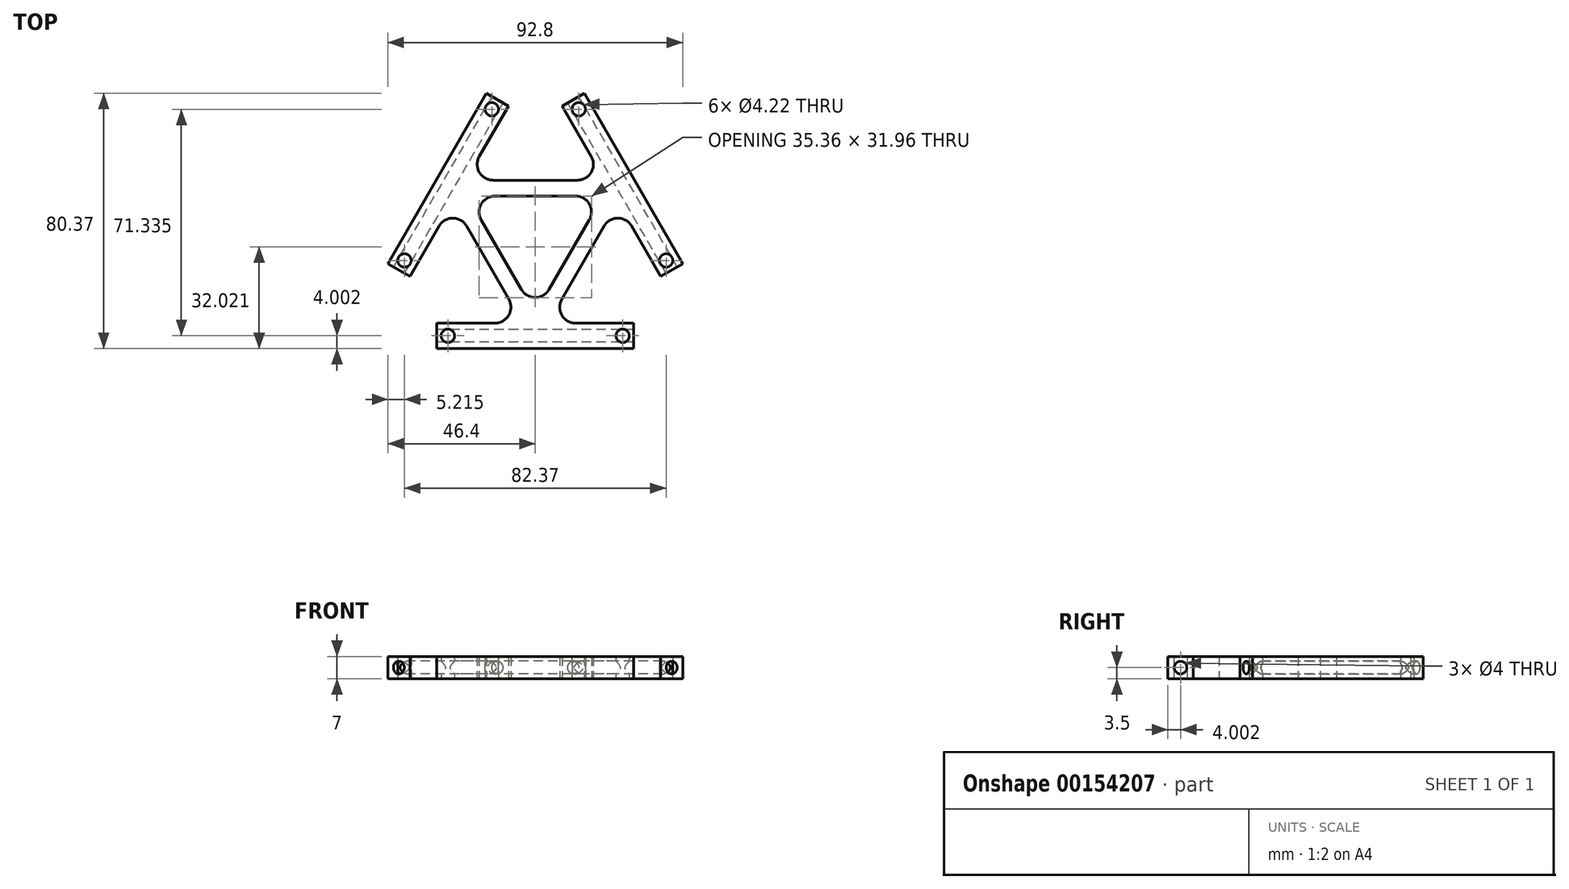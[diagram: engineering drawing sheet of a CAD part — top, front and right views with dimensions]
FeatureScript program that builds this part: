
annotation { "Feature Type Name" : "Feature", "Feature Type Description" : "" }
export const myFeature = defineFeature(function(context is Context, id is Id, definition is map)
    precondition{}
    {
        {
            var Q0;
            Q0=qCreatedBy(makeId("Top.planeOp"),FACE);
            var sketch = newSketch(context, id + "F0", { "sketchPlane" : qUnion([Q0])});
            skLineSegment(sketch, "E0", {"start": v(-8.35, 14.46) * mm, "end": v(-21.65, 37.5) * mm});
            skLineSegment(sketch, "E1", {"start": v(-13.3, 51.96) * mm, "end": v(13.3, 51.96) * mm});
            skLineSegment(sketch, "E2", {"start": v(21.65, 37.5) * mm, "end": v(8.35, 14.46) * mm});
            skLineSegment(sketch, "E3.bottom", {"start": v(-31, 6.96) * mm, "end": v(-12.68, 6.96) * mm});
            skLineSegment(sketch, "E3.top", {"start": v(-31, -1.04) * mm, "end": v(31, -1.04) * mm});
            skLineSegment(sketch, "E3.left", {"start": v(-31, 6.96) * mm, "end": v(-31, -1.04) * mm});
            skLineSegment(sketch, "E3.right", {"start": v(31, 6.96) * mm, "end": v(31, -1.04) * mm});
            skLineSegment(sketch, "E4", {"start": v(-15, 64.02) * mm, "end": v(-17.63, 59.46) * mm});
            skPoint(sketch, "E4.startSnap0", {"position": v(-15, 25.98) * mm});
            skLineSegment(sketch, "E5", {"start": v(-39.47, 21.63) * mm, "end": v(-46.4, 25.63) * mm});
            skLineSegment(sketch, "E6", {"start": v(-46.4, 25.63) * mm, "end": v(-15.4, 79.33) * mm});
            skLineSegment(sketch, "E7", {"start": v(-15.4, 79.33) * mm, "end": v(-8.47, 75.33) * mm});
            skLineSegment(sketch, "E8", {"start": v(39.47, 21.63) * mm, "end": v(30.31, 37.5) * mm});
            skLineSegment(sketch, "E9", {"start": v(8.47, 75.33) * mm, "end": v(15.4, 79.33) * mm});
            skLineSegment(sketch, "E10", {"start": v(15.4, 79.33) * mm, "end": v(46.4, 25.63) * mm});
            skLineSegment(sketch, "E11", {"start": v(46.4, 25.63) * mm, "end": v(39.47, 21.63) * mm});
            skLineSegment(sketch, "E12", {"start": v(-15, 64.02) * mm, "end": v(-8.47, 75.33) * mm});
            skPoint(sketch, "E13.orphan", {"position": v(-30, 51.96) * mm});
            skPoint(sketch, "E14.orphan", {"position": v(0, 0) * mm});
            skPoint(sketch, "E15.orphan", {"position": v(30, 51.96) * mm});
            skLineSegment(sketch, "E16.trimOffspring", {"start": v(-30.31, 37.5) * mm, "end": v(-39.47, 21.63) * mm});
            skLineSegment(sketch, "E17.trimOffspring", {"start": v(12.68, 6.96) * mm, "end": v(31, 6.96) * mm});
            skLineSegment(sketch, "E18.trimOffspring", {"start": v(17.63, 59.46) * mm, "end": v(8.47, 75.33) * mm});
            skCircle(sketch, "E19", {"center": v(-41.19, 26.67) * mm, "radius": 2.11 * mm});
            skCircle(sketch, "E20", {"center": v(-13.69, 74.3) * mm, "radius": 2.11 * mm});
            skCircle(sketch, "E21", {"center": v(13.69, 74.3) * mm, "radius": 2.11 * mm});
            skCircle(sketch, "E22", {"center": v(41.19, 26.67) * mm, "radius": 2.11 * mm});
            skCircle(sketch, "E23", {"center": v(27.5, 2.96) * mm, "radius": 2.11 * mm});
            skPoint(sketch, "E23.centerSnap0", {"position": v(31, 2.96) * mm});
            skCircle(sketch, "E24", {"center": v(-27.5, 2.96) * mm, "radius": 2.11 * mm});
            skPoint(sketch, "E24.centerSnap0", {"position": v(-31, 2.96) * mm});
            skLineSegment(sketch, "E25", {"start": v(-17, 39.46) * mm, "end": v(-4.33, 17.5) * mm});
            skLineSegment(sketch, "E26", {"start": v(4.33, 17.5) * mm, "end": v(17, 39.46) * mm});
            skLineSegment(sketch, "E27", {"start": v(12.68, 46.96) * mm, "end": v(-12.68, 46.96) * mm});
            skPoint(sketch, "E28.visualSharp", {"position": v(-21.34, 46.96) * mm});
            skArc(sketch, "E28.filletArc", {"start": v(-12.68, 46.96) * mm, "mid": v(-17, 44.46) * mm, "end": v(-17, 39.46) * mm});
            skPoint(sketch, "E29.visualSharp", {"position": v(21.34, 46.96) * mm});
            skArc(sketch, "E29.filletArc", {"start": v(17, 39.46) * mm, "mid": v(17, 44.46) * mm, "end": v(12.68, 46.96) * mm});
            skPoint(sketch, "E30.visualSharp", {"position": v(0, 10) * mm});
            skArc(sketch, "E30.filletArc", {"start": v(-4.33, 17.5) * mm, "mid": v(0, 15) * mm, "end": v(4.33, 17.5) * mm});
            skPoint(sketch, "E31.visualSharp", {"position": v(-4.02, 6.96) * mm});
            skArc(sketch, "E31.filletArc", {"start": v(-12.68, 6.96) * mm, "mid": v(-8.35, 9.46) * mm, "end": v(-8.35, 14.46) * mm});
            skPoint(sketch, "E32.visualSharp", {"position": v(-21.96, 51.96) * mm});
            skArc(sketch, "E32.filletArc", {"start": v(-17.63, 59.46) * mm, "mid": v(-17.63, 54.46) * mm, "end": v(-13.3, 51.96) * mm});
            skPoint(sketch, "E33.visualSharp", {"position": v(21.96, 51.96) * mm});
            skArc(sketch, "E33.filletArc", {"start": v(13.3, 51.96) * mm, "mid": v(17.63, 54.46) * mm, "end": v(17.63, 59.46) * mm});
            skPoint(sketch, "E34.visualSharp", {"position": v(25.98, 45) * mm});
            skArc(sketch, "E34.filletArc", {"start": v(30.31, 37.5) * mm, "mid": v(25.98, 40) * mm, "end": v(21.65, 37.5) * mm});
            skPoint(sketch, "E35.visualSharp", {"position": v(4.02, 6.96) * mm});
            skArc(sketch, "E35.filletArc", {"start": v(8.35, 14.46) * mm, "mid": v(8.35, 9.46) * mm, "end": v(12.68, 6.96) * mm});
            skPoint(sketch, "E36.visualSharp", {"position": v(-25.98, 45) * mm});
            skArc(sketch, "E36.filletArc", {"start": v(-21.65, 37.5) * mm, "mid": v(-25.98, 40) * mm, "end": v(-30.31, 37.5) * mm});
            skSolve(sketch);
        }
        {
            var Q0;
            Q0 = qSketchRegion(id + "F0", true);
            extrude(context, id + "F1", {"entities" : qUnion([Q0]), "depth" : 7 * mm});
        }
        {
            var Q0;
            Q0=makeQuery(id+"F1.opExtrude","SWEPT_FACE",FACE,{"disambiguationData":[OSD([sQuery(id+"F0.wireOp",EDGE,"E5")])]});
            var sketch = newSketch(context, id + "F2", { "sketchPlane" : qUnion([Q0])});
            skCircle(sketch, "E37", {"center": v(-49, 3.5) * mm, "radius": 2 * mm});
            skPoint(sketch, "E37.centerSnap0", {"position": v(-49, 7) * mm});
            skSolve(sketch);
        }
        {
            var Q0;
            Q0 = qSketchRegion(id + "F2", true);
            extrude(context, id + "F3", {"entities" : qUnion([Q0]), "operationType" : NewBodyOperationType.REMOVE, "endBound" : BoundingType.THROUGH_ALL, "oppositeDirection" : true, "depth" : 25 * mm});
        }
        {
            var Q0;
            Q0=makeQuery(id+"F1.opExtrude","SWEPT_FACE",FACE,{"disambiguationData":[OSD([sQuery(id+"F0.wireOp",EDGE,"E3.left")])]});
            var sketch = newSketch(context, id + "F4", { "sketchPlane" : qUnion([Q0])});
            skCircle(sketch, "E38", {"center": v(-2.96, 3.5) * mm, "radius": 2 * mm});
            skPoint(sketch, "E38.centerSnap0", {"position": v(1.04, 3.5) * mm});
            skSolve(sketch);
        }
        {
            var Q0;
            Q0=makeQuery(id+"F1.opExtrude","SWEPT_FACE",FACE,{"disambiguationData":[OSD([sQuery(id+"F0.wireOp",EDGE,"E9")])]});
            var sketch = newSketch(context, id + "F5", { "sketchPlane" : qUnion([Q0])});
            skCircle(sketch, "E39", {"center": v(-49, 3.5) * mm, "radius": 2 * mm});
            skPoint(sketch, "E39.centerSnap0", {"position": v(-49, 7) * mm});
            skSolve(sketch);
        }
        {
            var Q0;
            Q0 = qSketchRegion(id + "F4", true);
            extrude(context, id + "F6", {"entities" : qUnion([Q0]), "operationType" : NewBodyOperationType.REMOVE, "endBound" : BoundingType.THROUGH_ALL, "oppositeDirection" : true, "depth" : 25 * mm});
        }
        {
            var Q0;
            Q0 = qSketchRegion(id + "F5", true);
            extrude(context, id + "F7", {"entities" : qUnion([Q0]), "operationType" : NewBodyOperationType.REMOVE, "endBound" : BoundingType.THROUGH_ALL, "oppositeDirection" : true, "depth" : 25 * mm});
        }
    });
